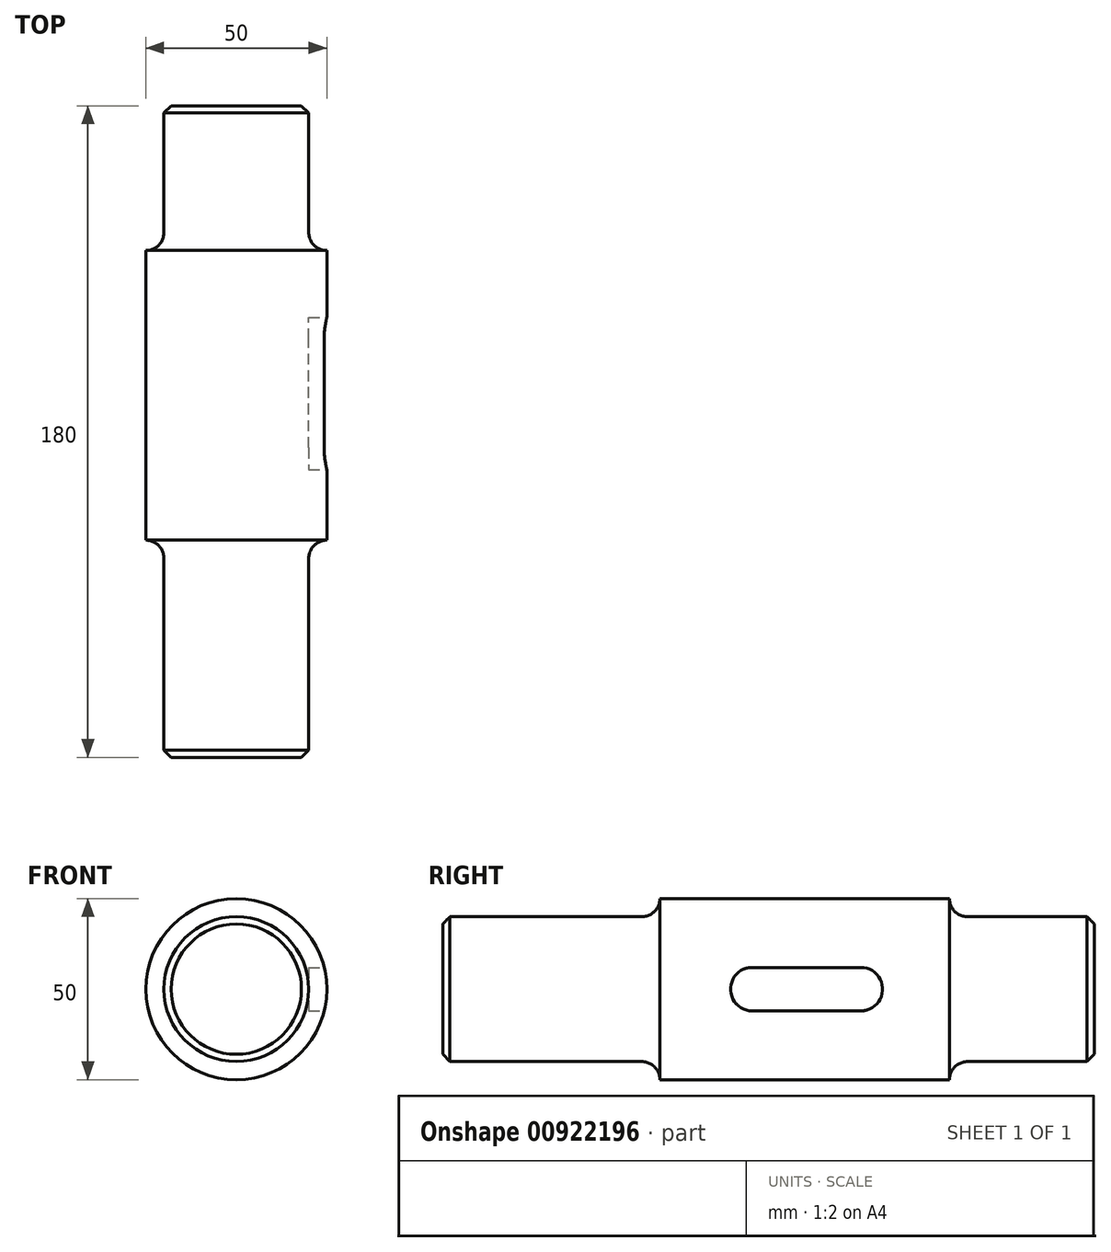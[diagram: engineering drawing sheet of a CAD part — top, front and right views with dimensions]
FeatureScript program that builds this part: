
annotation { "Feature Type Name" : "Feature", "Feature Type Description" : "" }
export const myFeature = defineFeature(function(context is Context, id is Id, definition is map)
    precondition{}
    {
        {
            var Q0;
            Q0=qCreatedBy(makeId("Right.planeOp"),FACE);
            var sketch = newSketch(context, id + "F0", { "sketchPlane" : qUnion([Q0])});
            skLineSegment(sketch, "E0", {"start": v(0, 25) * mm, "end": v(-71.97, 25) * mm});
            skLineSegment(sketch, "E1", {"start": v(-71.97, 25) * mm, "end": v(-71.97, 20) * mm});
            skLineSegment(sketch, "E2", {"start": v(-71.97, 20) * mm, "end": v(-131.97, 20) * mm});
            skLineSegment(sketch, "E3", {"start": v(-131.97, 20) * mm, "end": v(-131.97, 0) * mm});
            skLineSegment(sketch, "E4", {"start": v(0, 25) * mm, "end": v(8.03, 25) * mm});
            skLineSegment(sketch, "E5", {"start": v(8.03, 25) * mm, "end": v(8.03, 20) * mm});
            skLineSegment(sketch, "E6", {"start": v(8.03, 20) * mm, "end": v(48.03, 20) * mm});
            skLineSegment(sketch, "E7", {"start": v(48.03, 20) * mm, "end": v(48.03, 0) * mm});
            skLineSegment(sketch, "E8", {"start": v(-142.39, 0) * mm, "end": v(81.79, 0) * mm});
            skSolve(sketch);
        }
        {
            var Q0;
            Q0 = qSketchRegion(id + "F0", true);
            var Q1;
            Q1=sQuery(id+"F0.wireOp",EDGE,"E8");
            revolve(context, id + "F1", {"surfaceOperationType" : NewSurfaceOperationType.NEW, "entities" : qUnion([Q0]), "axis" : qUnion([Q1]), "revolveType" : RevolveType.FULL});
        }
        {
            var Q0;
            Q0=qCreatedBy(makeId("Right.planeOp"),FACE);
            cPlane(context, id + "F2", {"entities" : qUnion([Q0]), "cplaneType" : CPlaneType.OFFSET, "offset" : 25 * mm, "width" : 150 * mm, "height" : 150 * mm});
        }
        {
            var Q0;
            Q0=qCreatedBy(id+"F2.planeOp",FACE);
            var sketch = newSketch(context, id + "F3", { "sketchPlane" : qUnion([Q0])});
            skLineSegment(sketch, "E9.top", {"start": v(-46.44, 6) * mm, "end": v(-16.44, 6) * mm});
            skLineSegment(sketch, "E10.MirrorCS", {"start": v(-46.44, -6) * mm, "end": v(-16.44, -6) * mm});
            skArc(sketch, "E11", {"start": v(-46.44, 6) * mm, "mid": v(-52.44, 0) * mm, "end": v(-46.44, -6) * mm});
            skArc(sketch, "E12", {"start": v(-16.44, -6) * mm, "mid": v(-10.44, 0) * mm, "end": v(-16.44, 6) * mm});
            skSolve(sketch);
        }
        {
            var Q0;
            Q0=makeQuery(id+"F1.opRevolve","SWEPT_EDGE",EDGE,{"disambiguationData":[OSD([sQuery(id+"F0.wireOp",EDGE,"E2"),sQuery(id+"F0.wireOp",EDGE,"E3")])]});
            var Q1;
            Q1=makeQuery(id+"F1.opRevolve","SWEPT_EDGE",EDGE,{"disambiguationData":[OSD([sQuery(id+"F0.wireOp",EDGE,"E6"),sQuery(id+"F0.wireOp",EDGE,"E7")])]});
            chamfer(context, id + "F4", {"entities" : qUnion([Q0, Q1]), "width" : 2 * mm, "tangentPropagation" : true});
        }
        {
            var Q0;
            Q0=makeQuery(id+"F1.opRevolve","SWEPT_EDGE",EDGE,{"disambiguationData":[OSD([sQuery(id+"F0.wireOp",EDGE,"E1"),sQuery(id+"F0.wireOp",EDGE,"E2")])]});
            var Q1;
            Q1=makeQuery(id+"F1.opRevolve","SWEPT_EDGE",EDGE,{"disambiguationData":[OSD([sQuery(id+"F0.wireOp",EDGE,"E5"),sQuery(id+"F0.wireOp",EDGE,"E6")])]});
            fillet(context, id + "F5", {"entities" : qUnion([Q0, Q1]), "radius" : 5 * mm, "tangentPropagation" : true, "allowEdgeOverflow" : false});
        }
        {
            var Q0;
            Q0=makeQuery(id+"F3.imprint","IMPRINT",FACE,{"disambiguationData":[TD([[makeQuery(id+"F3.imprint","IMPRINT",EDGE,{"derivedFrom":sQuery(id+"F3.wireOp",EDGE,"E9.top")}),-1.0]])]});
            extrude(context, id + "F6", {"entities" : qUnion([Q0]), "operationType" : NewBodyOperationType.REMOVE, "oppositeDirection" : true, "depth" : 5 * mm, "offsetDistance" : 25 * mm});
        }
    });
